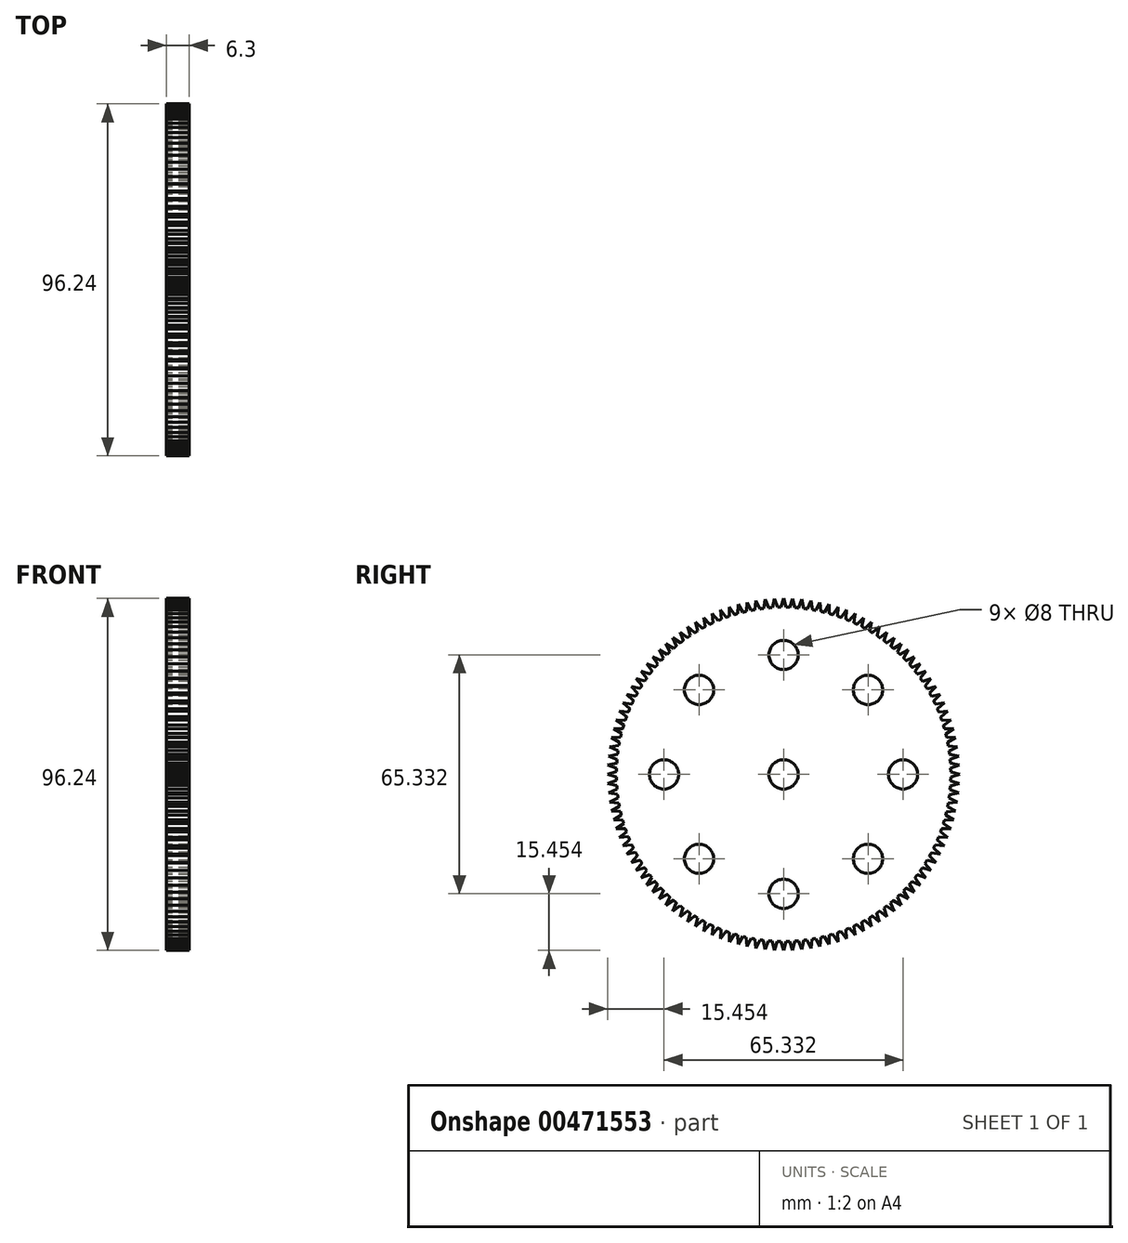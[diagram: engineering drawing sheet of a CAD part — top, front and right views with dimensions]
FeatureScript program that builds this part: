
annotation { "Feature Type Name" : "Feature", "Feature Type Description" : "" }
export const myFeature = defineFeature(function(context is Context, id is Id, definition is map)
    precondition{}
    {
        {
            var Q0;
            Q0=qCreatedBy(makeId("Right.planeOp"),FACE);
            var sketch = newSketch(context, id + "F0", { "sketchPlane" : qUnion([Q0])});
            skCircle(sketch, "E0", {"center": v(0, 0) * mm, "radius": 45.72 * mm});
            skCircle(sketch, "E1", {"center": v(0, 32.67) * mm, "radius": 4 * mm});
            skCircle(sketch, "E2.1.0", {"center": v(-23.1, 23.1) * mm, "radius": 4 * mm});
            skCircle(sketch, "E2.2.0", {"center": v(-32.67, 0) * mm, "radius": 4 * mm});
            skCircle(sketch, "E2.3.0", {"center": v(-23.1, -23.1) * mm, "radius": 4 * mm});
            skCircle(sketch, "E2.4.0", {"center": v(0, -32.67) * mm, "radius": 4 * mm});
            skCircle(sketch, "E2.5.0", {"center": v(23.1, -23.1) * mm, "radius": 4 * mm});
            skCircle(sketch, "E2.6.0", {"center": v(32.67, 0) * mm, "radius": 4 * mm});
            skCircle(sketch, "E2.7.0", {"center": v(23.1, 23.1) * mm, "radius": 4 * mm});
            skCircle(sketch, "E3", {"center": v(0, 0) * mm, "radius": 4 * mm});
            skSolve(sketch);
        }
        {
            var Q0;
            Q0=makeQuery(id+"F0.imprint","IMPRINT",FACE,{"disambiguationData":[TD([[makeQuery(id+"F0.imprint","IMPRINT",EDGE,{"derivedFrom":sQuery(id+"F0.wireOp",EDGE,"E0")}),1.0]])]});
            extrude(context, id + "F1", {"entities" : qUnion([Q0]), "depth" : 6.3 * mm});
        }
        {
            var Q0;
            Q0=qCreatedBy(makeId("Right.planeOp"),FACE);
            var sketch = newSketch(context, id + "F2", { "sketchPlane" : qUnion([Q0])});
            skLineSegment(sketch, "E4", {"start": v(-45.69, 0.74) * mm, "end": v(-48.12, 0) * mm});
            skLineSegment(sketch, "E5", {"start": v(-48.12, 0) * mm, "end": v(-45.69, -0.69) * mm});
            skLineSegment(sketch, "E6.1.0", {"start": v(-45.67, -1.65) * mm, "end": v(-48.06, -2.52) * mm});
            skLineSegment(sketch, "E6.2.0", {"start": v(-45.52, -4.04) * mm, "end": v(-47.86, -5.03) * mm});
            skLineSegment(sketch, "E6.3.0", {"start": v(-45.24, -6.42) * mm, "end": v(-47.53, -7.53) * mm});
            skLineSegment(sketch, "E6.4.0", {"start": v(-44.85, -8.78) * mm, "end": v(-47.07, -10) * mm});
            skLineSegment(sketch, "E6.5.0", {"start": v(-44.32, -11.11) * mm, "end": v(-46.48, -12.46) * mm});
            skLineSegment(sketch, "E6.6.0", {"start": v(-43.68, -13.42) * mm, "end": v(-45.77, -14.87) * mm});
            skLineSegment(sketch, "E6.7.0", {"start": v(-42.92, -15.68) * mm, "end": v(-44.93, -17.25) * mm});
            skLineSegment(sketch, "E6.8.0", {"start": v(-42.04, -17.9) * mm, "end": v(-43.96, -19.57) * mm});
            skLineSegment(sketch, "E6.9.0", {"start": v(-41.05, -20.08) * mm, "end": v(-42.88, -21.85) * mm});
            skLineSegment(sketch, "E6.10.0", {"start": v(-39.94, -22.2) * mm, "end": v(-41.68, -24.06) * mm});
            skLineSegment(sketch, "E6.11.0", {"start": v(-38.72, -24.26) * mm, "end": v(-40.36, -26.21) * mm});
            skLineSegment(sketch, "E6.12.0", {"start": v(-37.4, -26.26) * mm, "end": v(-38.93, -28.29) * mm});
            skLineSegment(sketch, "E6.13.0", {"start": v(-35.97, -28.18) * mm, "end": v(-37.4, -30.29) * mm});
            skLineSegment(sketch, "E6.14.0", {"start": v(-34.45, -30.02) * mm, "end": v(-35.76, -32.2) * mm});
            skLineSegment(sketch, "E6.15.0", {"start": v(-32.83, -31.78) * mm, "end": v(-34.03, -34.03) * mm});
            skLineSegment(sketch, "E6.16.0", {"start": v(-31.12, -33.46) * mm, "end": v(-32.2, -35.76) * mm});
            skLineSegment(sketch, "E6.17.0", {"start": v(-29.33, -35.04) * mm, "end": v(-30.29, -37.4) * mm});
            skLineSegment(sketch, "E6.18.0", {"start": v(-27.45, -36.53) * mm, "end": v(-28.29, -38.93) * mm});
            skLineSegment(sketch, "E6.19.0", {"start": v(-25.5, -37.92) * mm, "end": v(-26.21, -40.36) * mm});
            skLineSegment(sketch, "E6.20.0", {"start": v(-23.49, -39.2) * mm, "end": v(-24.06, -41.68) * mm});
            skLineSegment(sketch, "E6.21.0", {"start": v(-21.4, -40.37) * mm, "end": v(-21.85, -42.88) * mm});
            skLineSegment(sketch, "E6.22.0", {"start": v(-19.26, -41.44) * mm, "end": v(-19.57, -43.96) * mm});
            skLineSegment(sketch, "E6.23.0", {"start": v(-17.06, -42.4) * mm, "end": v(-17.25, -44.93) * mm});
            skLineSegment(sketch, "E6.24.0", {"start": v(-14.82, -43.23) * mm, "end": v(-14.87, -45.77) * mm});
            skLineSegment(sketch, "E6.25.0", {"start": v(-12.54, -43.94) * mm, "end": v(-12.46, -46.48) * mm});
            skLineSegment(sketch, "E6.26.0", {"start": v(-10.22, -44.54) * mm, "end": v(-10, -47.07) * mm});
            skLineSegment(sketch, "E6.27.0", {"start": v(-7.88, -45.01) * mm, "end": v(-7.53, -47.53) * mm});
            skLineSegment(sketch, "E6.28.0", {"start": v(-5.51, -45.36) * mm, "end": v(-5.03, -47.86) * mm});
            skLineSegment(sketch, "E6.29.0", {"start": v(-3.13, -45.59) * mm, "end": v(-2.52, -48.06) * mm});
            skLineSegment(sketch, "E6.30.0", {"start": v(-0.74, -45.69) * mm, "end": v(0, -48.12) * mm});
            skLineSegment(sketch, "E6.31.0", {"start": v(1.65, -45.67) * mm, "end": v(2.52, -48.06) * mm});
            skLineSegment(sketch, "E6.32.0", {"start": v(4.04, -45.52) * mm, "end": v(5.03, -47.86) * mm});
            skLineSegment(sketch, "E6.33.0", {"start": v(6.42, -45.24) * mm, "end": v(7.53, -47.53) * mm});
            skLineSegment(sketch, "E6.34.0", {"start": v(8.78, -44.85) * mm, "end": v(10, -47.07) * mm});
            skLineSegment(sketch, "E6.35.0", {"start": v(11.11, -44.32) * mm, "end": v(12.46, -46.48) * mm});
            skLineSegment(sketch, "E6.36.0", {"start": v(13.42, -43.68) * mm, "end": v(14.87, -45.77) * mm});
            skLineSegment(sketch, "E6.37.0", {"start": v(15.68, -42.92) * mm, "end": v(17.25, -44.93) * mm});
            skLineSegment(sketch, "E6.38.0", {"start": v(17.9, -42.04) * mm, "end": v(19.57, -43.96) * mm});
            skLineSegment(sketch, "E6.39.0", {"start": v(20.08, -41.05) * mm, "end": v(21.85, -42.88) * mm});
            skLineSegment(sketch, "E6.40.0", {"start": v(22.2, -39.94) * mm, "end": v(24.06, -41.68) * mm});
            skLineSegment(sketch, "E6.41.0", {"start": v(24.26, -38.72) * mm, "end": v(26.21, -40.36) * mm});
            skLineSegment(sketch, "E6.42.0", {"start": v(26.26, -37.4) * mm, "end": v(28.29, -38.93) * mm});
            skLineSegment(sketch, "E6.43.0", {"start": v(28.18, -35.97) * mm, "end": v(30.29, -37.4) * mm});
            skLineSegment(sketch, "E6.44.0", {"start": v(30.02, -34.45) * mm, "end": v(32.2, -35.76) * mm});
            skLineSegment(sketch, "E6.45.0", {"start": v(31.78, -32.83) * mm, "end": v(34.03, -34.03) * mm});
            skLineSegment(sketch, "E6.46.0", {"start": v(33.46, -31.12) * mm, "end": v(35.76, -32.2) * mm});
            skLineSegment(sketch, "E6.47.0", {"start": v(35.04, -29.33) * mm, "end": v(37.4, -30.29) * mm});
            skLineSegment(sketch, "E6.48.0", {"start": v(36.53, -27.45) * mm, "end": v(38.93, -28.29) * mm});
            skLineSegment(sketch, "E6.49.0", {"start": v(37.92, -25.5) * mm, "end": v(40.36, -26.21) * mm});
            skLineSegment(sketch, "E6.50.0", {"start": v(39.2, -23.49) * mm, "end": v(41.68, -24.06) * mm});
            skLineSegment(sketch, "E6.51.0", {"start": v(40.37, -21.4) * mm, "end": v(42.88, -21.85) * mm});
            skLineSegment(sketch, "E6.52.0", {"start": v(41.44, -19.26) * mm, "end": v(43.96, -19.57) * mm});
            skLineSegment(sketch, "E6.53.0", {"start": v(42.4, -17.06) * mm, "end": v(44.93, -17.25) * mm});
            skLineSegment(sketch, "E6.54.0", {"start": v(43.23, -14.82) * mm, "end": v(45.77, -14.87) * mm});
            skLineSegment(sketch, "E6.55.0", {"start": v(43.94, -12.54) * mm, "end": v(46.48, -12.46) * mm});
            skLineSegment(sketch, "E6.56.0", {"start": v(44.54, -10.22) * mm, "end": v(47.07, -10) * mm});
            skLineSegment(sketch, "E6.57.0", {"start": v(45.01, -7.88) * mm, "end": v(47.53, -7.53) * mm});
            skLineSegment(sketch, "E6.58.0", {"start": v(45.36, -5.51) * mm, "end": v(47.86, -5.03) * mm});
            skLineSegment(sketch, "E6.59.0", {"start": v(45.59, -3.13) * mm, "end": v(48.06, -2.52) * mm});
            skLineSegment(sketch, "E6.60.0", {"start": v(45.69, -0.74) * mm, "end": v(48.12, 0) * mm});
            skLineSegment(sketch, "E6.61.0", {"start": v(45.67, 1.65) * mm, "end": v(48.06, 2.52) * mm});
            skLineSegment(sketch, "E6.62.0", {"start": v(45.52, 4.04) * mm, "end": v(47.86, 5.03) * mm});
            skLineSegment(sketch, "E6.63.0", {"start": v(45.24, 6.42) * mm, "end": v(47.53, 7.53) * mm});
            skLineSegment(sketch, "E6.64.0", {"start": v(44.85, 8.78) * mm, "end": v(47.07, 10) * mm});
            skLineSegment(sketch, "E6.65.0", {"start": v(44.32, 11.11) * mm, "end": v(46.48, 12.46) * mm});
            skLineSegment(sketch, "E6.66.0", {"start": v(43.68, 13.42) * mm, "end": v(45.77, 14.87) * mm});
            skLineSegment(sketch, "E6.67.0", {"start": v(42.92, 15.68) * mm, "end": v(44.93, 17.25) * mm});
            skLineSegment(sketch, "E6.68.0", {"start": v(42.04, 17.9) * mm, "end": v(43.96, 19.57) * mm});
            skLineSegment(sketch, "E6.69.0", {"start": v(41.05, 20.08) * mm, "end": v(42.88, 21.85) * mm});
            skLineSegment(sketch, "E6.70.0", {"start": v(39.94, 22.2) * mm, "end": v(41.68, 24.06) * mm});
            skLineSegment(sketch, "E6.71.0", {"start": v(38.72, 24.26) * mm, "end": v(40.36, 26.21) * mm});
            skLineSegment(sketch, "E6.72.0", {"start": v(37.4, 26.26) * mm, "end": v(38.93, 28.29) * mm});
            skLineSegment(sketch, "E6.73.0", {"start": v(35.97, 28.18) * mm, "end": v(37.4, 30.29) * mm});
            skLineSegment(sketch, "E6.74.0", {"start": v(34.45, 30.02) * mm, "end": v(35.76, 32.2) * mm});
            skLineSegment(sketch, "E6.75.0", {"start": v(32.83, 31.78) * mm, "end": v(34.03, 34.03) * mm});
            skLineSegment(sketch, "E6.76.0", {"start": v(31.12, 33.46) * mm, "end": v(32.2, 35.76) * mm});
            skLineSegment(sketch, "E6.77.0", {"start": v(29.33, 35.04) * mm, "end": v(30.29, 37.4) * mm});
            skLineSegment(sketch, "E6.78.0", {"start": v(27.45, 36.53) * mm, "end": v(28.29, 38.93) * mm});
            skLineSegment(sketch, "E6.79.0", {"start": v(25.5, 37.92) * mm, "end": v(26.21, 40.36) * mm});
            skLineSegment(sketch, "E6.80.0", {"start": v(23.49, 39.2) * mm, "end": v(24.06, 41.68) * mm});
            skLineSegment(sketch, "E6.81.0", {"start": v(21.4, 40.37) * mm, "end": v(21.85, 42.88) * mm});
            skLineSegment(sketch, "E6.82.0", {"start": v(19.26, 41.44) * mm, "end": v(19.57, 43.96) * mm});
            skLineSegment(sketch, "E6.83.0", {"start": v(17.06, 42.4) * mm, "end": v(17.25, 44.93) * mm});
            skLineSegment(sketch, "E6.84.0", {"start": v(14.82, 43.23) * mm, "end": v(14.87, 45.77) * mm});
            skLineSegment(sketch, "E6.85.0", {"start": v(12.54, 43.94) * mm, "end": v(12.46, 46.48) * mm});
            skLineSegment(sketch, "E6.86.0", {"start": v(10.22, 44.54) * mm, "end": v(10, 47.07) * mm});
            skLineSegment(sketch, "E6.87.0", {"start": v(7.88, 45.01) * mm, "end": v(7.53, 47.53) * mm});
            skLineSegment(sketch, "E6.88.0", {"start": v(5.51, 45.36) * mm, "end": v(5.03, 47.86) * mm});
            skLineSegment(sketch, "E6.89.0", {"start": v(3.13, 45.59) * mm, "end": v(2.52, 48.06) * mm});
            skLineSegment(sketch, "E6.90.0", {"start": v(0.74, 45.69) * mm, "end": v(0, 48.12) * mm});
            skLineSegment(sketch, "E6.91.0", {"start": v(-1.65, 45.67) * mm, "end": v(-2.52, 48.06) * mm});
            skLineSegment(sketch, "E6.92.0", {"start": v(-4.04, 45.52) * mm, "end": v(-5.03, 47.86) * mm});
            skLineSegment(sketch, "E6.93.0", {"start": v(-6.42, 45.24) * mm, "end": v(-7.53, 47.53) * mm});
            skLineSegment(sketch, "E6.94.0", {"start": v(-8.78, 44.85) * mm, "end": v(-10, 47.07) * mm});
            skLineSegment(sketch, "E6.95.0", {"start": v(-11.11, 44.32) * mm, "end": v(-12.46, 46.48) * mm});
            skLineSegment(sketch, "E6.96.0", {"start": v(-13.42, 43.68) * mm, "end": v(-14.87, 45.77) * mm});
            skLineSegment(sketch, "E6.97.0", {"start": v(-15.68, 42.92) * mm, "end": v(-17.25, 44.93) * mm});
            skLineSegment(sketch, "E6.98.0", {"start": v(-17.9, 42.04) * mm, "end": v(-19.57, 43.96) * mm});
            skLineSegment(sketch, "E6.99.0", {"start": v(-20.08, 41.05) * mm, "end": v(-21.85, 42.88) * mm});
            skLineSegment(sketch, "E6.100.0", {"start": v(-22.2, 39.94) * mm, "end": v(-24.06, 41.68) * mm});
            skLineSegment(sketch, "E6.101.0", {"start": v(-24.26, 38.72) * mm, "end": v(-26.21, 40.36) * mm});
            skLineSegment(sketch, "E6.102.0", {"start": v(-26.26, 37.4) * mm, "end": v(-28.29, 38.93) * mm});
            skLineSegment(sketch, "E6.103.0", {"start": v(-28.18, 35.97) * mm, "end": v(-30.29, 37.4) * mm});
            skLineSegment(sketch, "E6.104.0", {"start": v(-30.02, 34.45) * mm, "end": v(-32.2, 35.76) * mm});
            skLineSegment(sketch, "E6.105.0", {"start": v(-31.78, 32.83) * mm, "end": v(-34.03, 34.03) * mm});
            skLineSegment(sketch, "E6.106.0", {"start": v(-33.46, 31.12) * mm, "end": v(-35.76, 32.2) * mm});
            skLineSegment(sketch, "E6.107.0", {"start": v(-35.04, 29.33) * mm, "end": v(-37.4, 30.29) * mm});
            skLineSegment(sketch, "E6.108.0", {"start": v(-36.53, 27.45) * mm, "end": v(-38.93, 28.29) * mm});
            skLineSegment(sketch, "E6.109.0", {"start": v(-37.92, 25.5) * mm, "end": v(-40.36, 26.21) * mm});
            skLineSegment(sketch, "E6.110.0", {"start": v(-39.2, 23.49) * mm, "end": v(-41.68, 24.06) * mm});
            skLineSegment(sketch, "E6.111.0", {"start": v(-40.37, 21.4) * mm, "end": v(-42.88, 21.85) * mm});
            skLineSegment(sketch, "E6.112.0", {"start": v(-41.44, 19.26) * mm, "end": v(-43.96, 19.57) * mm});
            skLineSegment(sketch, "E6.113.0", {"start": v(-42.4, 17.06) * mm, "end": v(-44.93, 17.25) * mm});
            skLineSegment(sketch, "E6.114.0", {"start": v(-43.23, 14.82) * mm, "end": v(-45.77, 14.87) * mm});
            skLineSegment(sketch, "E6.115.0", {"start": v(-43.94, 12.54) * mm, "end": v(-46.48, 12.46) * mm});
            skLineSegment(sketch, "E6.116.0", {"start": v(-44.54, 10.22) * mm, "end": v(-47.07, 10) * mm});
            skLineSegment(sketch, "E6.117.0", {"start": v(-45.01, 7.88) * mm, "end": v(-47.53, 7.53) * mm});
            skLineSegment(sketch, "E6.118.0", {"start": v(-45.36, 5.51) * mm, "end": v(-47.86, 5.03) * mm});
            skLineSegment(sketch, "E6.119.0", {"start": v(-45.59, 3.13) * mm, "end": v(-48.06, 2.52) * mm});
            skPoint(sketch, "E6.center", {"position": v(0, 0) * mm});
            skLineSegment(sketch, "E7.1.0", {"start": v(-48.06, -2.52) * mm, "end": v(-45.6, -3.08) * mm});
            skLineSegment(sketch, "E7.2.0", {"start": v(-47.86, -5.03) * mm, "end": v(-45.37, -5.46) * mm});
            skLineSegment(sketch, "E7.3.0", {"start": v(-47.53, -7.53) * mm, "end": v(-45.02, -7.82) * mm});
            skLineSegment(sketch, "E7.4.0", {"start": v(-47.07, -10) * mm, "end": v(-44.55, -10.17) * mm});
            skLineSegment(sketch, "E7.5.0", {"start": v(-46.48, -12.46) * mm, "end": v(-43.96, -12.49) * mm});
            skLineSegment(sketch, "E7.6.0", {"start": v(-45.77, -14.87) * mm, "end": v(-43.24, -14.77) * mm});
            skLineSegment(sketch, "E7.7.0", {"start": v(-44.93, -17.25) * mm, "end": v(-42.4, -17.01) * mm});
            skLineSegment(sketch, "E7.8.0", {"start": v(-43.96, -19.57) * mm, "end": v(-41.46, -19.21) * mm});
            skLineSegment(sketch, "E7.9.0", {"start": v(-42.88, -21.85) * mm, "end": v(-40.4, -21.35) * mm});
            skLineSegment(sketch, "E7.10.0", {"start": v(-41.68, -24.06) * mm, "end": v(-39.23, -23.44) * mm});
            skLineSegment(sketch, "E7.11.0", {"start": v(-40.36, -26.21) * mm, "end": v(-37.95, -25.46) * mm});
            skLineSegment(sketch, "E7.12.0", {"start": v(-38.93, -28.29) * mm, "end": v(-36.56, -27.41) * mm});
            skLineSegment(sketch, "E7.13.0", {"start": v(-37.4, -30.29) * mm, "end": v(-35.08, -29.29) * mm});
            skLineSegment(sketch, "E7.14.0", {"start": v(-35.76, -32.2) * mm, "end": v(-33.5, -31.08) * mm});
            skLineSegment(sketch, "E7.15.0", {"start": v(-34.03, -34.03) * mm, "end": v(-31.82, -32.8) * mm});
            skLineSegment(sketch, "E7.16.0", {"start": v(-32.2, -35.76) * mm, "end": v(-30.06, -34.41) * mm});
            skLineSegment(sketch, "E7.17.0", {"start": v(-30.29, -37.4) * mm, "end": v(-28.22, -35.94) * mm});
            skLineSegment(sketch, "E7.18.0", {"start": v(-28.29, -38.93) * mm, "end": v(-26.3, -37.37) * mm});
            skLineSegment(sketch, "E7.19.0", {"start": v(-26.21, -40.36) * mm, "end": v(-24.3, -38.7) * mm});
            skLineSegment(sketch, "E7.20.0", {"start": v(-24.06, -41.68) * mm, "end": v(-22.25, -39.91) * mm});
            skLineSegment(sketch, "E7.21.0", {"start": v(-21.85, -42.88) * mm, "end": v(-20.13, -41.02) * mm});
            skLineSegment(sketch, "E7.22.0", {"start": v(-19.57, -43.96) * mm, "end": v(-17.96, -42.02) * mm});
            skLineSegment(sketch, "E7.23.0", {"start": v(-17.25, -44.93) * mm, "end": v(-15.73, -42.9) * mm});
            skLineSegment(sketch, "E7.24.0", {"start": v(-14.87, -45.77) * mm, "end": v(-13.47, -43.67) * mm});
            skLineSegment(sketch, "E7.25.0", {"start": v(-12.46, -46.48) * mm, "end": v(-11.16, -44.31) * mm});
            skLineSegment(sketch, "E7.26.0", {"start": v(-10, -47.07) * mm, "end": v(-8.83, -44.83) * mm});
            skLineSegment(sketch, "E7.27.0", {"start": v(-7.53, -47.53) * mm, "end": v(-6.47, -45.23) * mm});
            skLineSegment(sketch, "E7.28.0", {"start": v(-5.03, -47.86) * mm, "end": v(-4.1, -45.51) * mm});
            skLineSegment(sketch, "E7.29.0", {"start": v(-2.52, -48.06) * mm, "end": v(-1.7, -45.66) * mm});
            skLineSegment(sketch, "E7.30.0", {"start": v(0, -48.12) * mm, "end": v(0.69, -45.69) * mm});
            skLineSegment(sketch, "E7.31.0", {"start": v(2.52, -48.06) * mm, "end": v(3.08, -45.6) * mm});
            skLineSegment(sketch, "E7.32.0", {"start": v(5.03, -47.86) * mm, "end": v(5.46, -45.37) * mm});
            skLineSegment(sketch, "E7.33.0", {"start": v(7.53, -47.53) * mm, "end": v(7.82, -45.02) * mm});
            skLineSegment(sketch, "E7.34.0", {"start": v(10, -47.07) * mm, "end": v(10.17, -44.55) * mm});
            skLineSegment(sketch, "E7.35.0", {"start": v(12.46, -46.48) * mm, "end": v(12.49, -43.96) * mm});
            skLineSegment(sketch, "E7.36.0", {"start": v(14.87, -45.77) * mm, "end": v(14.77, -43.24) * mm});
            skLineSegment(sketch, "E7.37.0", {"start": v(17.25, -44.93) * mm, "end": v(17.01, -42.4) * mm});
            skLineSegment(sketch, "E7.38.0", {"start": v(19.57, -43.96) * mm, "end": v(19.21, -41.46) * mm});
            skLineSegment(sketch, "E7.39.0", {"start": v(21.85, -42.88) * mm, "end": v(21.35, -40.4) * mm});
            skLineSegment(sketch, "E7.40.0", {"start": v(24.06, -41.68) * mm, "end": v(23.44, -39.23) * mm});
            skLineSegment(sketch, "E7.41.0", {"start": v(26.21, -40.36) * mm, "end": v(25.46, -37.95) * mm});
            skLineSegment(sketch, "E7.42.0", {"start": v(28.29, -38.93) * mm, "end": v(27.41, -36.56) * mm});
            skLineSegment(sketch, "E7.43.0", {"start": v(30.29, -37.4) * mm, "end": v(29.29, -35.08) * mm});
            skLineSegment(sketch, "E7.44.0", {"start": v(32.2, -35.76) * mm, "end": v(31.08, -33.5) * mm});
            skLineSegment(sketch, "E7.45.0", {"start": v(34.03, -34.03) * mm, "end": v(32.8, -31.82) * mm});
            skLineSegment(sketch, "E7.46.0", {"start": v(35.76, -32.2) * mm, "end": v(34.41, -30.06) * mm});
            skLineSegment(sketch, "E7.47.0", {"start": v(37.4, -30.29) * mm, "end": v(35.94, -28.22) * mm});
            skLineSegment(sketch, "E7.48.0", {"start": v(38.93, -28.29) * mm, "end": v(37.37, -26.3) * mm});
            skLineSegment(sketch, "E7.49.0", {"start": v(40.36, -26.21) * mm, "end": v(38.7, -24.3) * mm});
            skLineSegment(sketch, "E7.50.0", {"start": v(41.68, -24.06) * mm, "end": v(39.91, -22.25) * mm});
            skLineSegment(sketch, "E7.51.0", {"start": v(42.88, -21.85) * mm, "end": v(41.02, -20.13) * mm});
            skLineSegment(sketch, "E7.52.0", {"start": v(43.96, -19.57) * mm, "end": v(42.02, -17.96) * mm});
            skLineSegment(sketch, "E7.53.0", {"start": v(44.93, -17.25) * mm, "end": v(42.9, -15.73) * mm});
            skLineSegment(sketch, "E7.54.0", {"start": v(45.77, -14.87) * mm, "end": v(43.67, -13.47) * mm});
            skLineSegment(sketch, "E7.55.0", {"start": v(46.48, -12.46) * mm, "end": v(44.31, -11.16) * mm});
            skLineSegment(sketch, "E7.56.0", {"start": v(47.07, -10) * mm, "end": v(44.83, -8.83) * mm});
            skLineSegment(sketch, "E7.57.0", {"start": v(47.53, -7.53) * mm, "end": v(45.23, -6.47) * mm});
            skLineSegment(sketch, "E7.58.0", {"start": v(47.86, -5.03) * mm, "end": v(45.51, -4.1) * mm});
            skLineSegment(sketch, "E7.59.0", {"start": v(48.06, -2.52) * mm, "end": v(45.66, -1.7) * mm});
            skLineSegment(sketch, "E7.60.0", {"start": v(48.12, 0) * mm, "end": v(45.69, 0.69) * mm});
            skLineSegment(sketch, "E7.61.0", {"start": v(48.06, 2.52) * mm, "end": v(45.6, 3.08) * mm});
            skLineSegment(sketch, "E7.62.0", {"start": v(47.86, 5.03) * mm, "end": v(45.37, 5.46) * mm});
            skLineSegment(sketch, "E7.63.0", {"start": v(47.53, 7.53) * mm, "end": v(45.02, 7.82) * mm});
            skLineSegment(sketch, "E7.64.0", {"start": v(47.07, 10) * mm, "end": v(44.55, 10.17) * mm});
            skLineSegment(sketch, "E7.65.0", {"start": v(46.48, 12.46) * mm, "end": v(43.96, 12.49) * mm});
            skLineSegment(sketch, "E7.66.0", {"start": v(45.77, 14.87) * mm, "end": v(43.24, 14.77) * mm});
            skLineSegment(sketch, "E7.67.0", {"start": v(44.93, 17.25) * mm, "end": v(42.4, 17.01) * mm});
            skLineSegment(sketch, "E7.68.0", {"start": v(43.96, 19.57) * mm, "end": v(41.46, 19.21) * mm});
            skLineSegment(sketch, "E7.69.0", {"start": v(42.88, 21.85) * mm, "end": v(40.4, 21.35) * mm});
            skLineSegment(sketch, "E7.70.0", {"start": v(41.68, 24.06) * mm, "end": v(39.23, 23.44) * mm});
            skLineSegment(sketch, "E7.71.0", {"start": v(40.36, 26.21) * mm, "end": v(37.95, 25.46) * mm});
            skLineSegment(sketch, "E7.72.0", {"start": v(38.93, 28.29) * mm, "end": v(36.56, 27.41) * mm});
            skLineSegment(sketch, "E7.73.0", {"start": v(37.4, 30.29) * mm, "end": v(35.08, 29.29) * mm});
            skLineSegment(sketch, "E7.74.0", {"start": v(35.76, 32.2) * mm, "end": v(33.5, 31.08) * mm});
            skLineSegment(sketch, "E7.75.0", {"start": v(34.03, 34.03) * mm, "end": v(31.82, 32.8) * mm});
            skLineSegment(sketch, "E7.76.0", {"start": v(32.2, 35.76) * mm, "end": v(30.06, 34.41) * mm});
            skLineSegment(sketch, "E7.77.0", {"start": v(30.29, 37.4) * mm, "end": v(28.22, 35.94) * mm});
            skLineSegment(sketch, "E7.78.0", {"start": v(28.29, 38.93) * mm, "end": v(26.3, 37.37) * mm});
            skLineSegment(sketch, "E7.79.0", {"start": v(26.21, 40.36) * mm, "end": v(24.3, 38.7) * mm});
            skLineSegment(sketch, "E7.80.0", {"start": v(24.06, 41.68) * mm, "end": v(22.25, 39.91) * mm});
            skLineSegment(sketch, "E7.81.0", {"start": v(21.85, 42.88) * mm, "end": v(20.13, 41.02) * mm});
            skLineSegment(sketch, "E7.82.0", {"start": v(19.57, 43.96) * mm, "end": v(17.96, 42.02) * mm});
            skLineSegment(sketch, "E7.83.0", {"start": v(17.25, 44.93) * mm, "end": v(15.73, 42.9) * mm});
            skLineSegment(sketch, "E7.84.0", {"start": v(14.87, 45.77) * mm, "end": v(13.47, 43.67) * mm});
            skLineSegment(sketch, "E7.85.0", {"start": v(12.46, 46.48) * mm, "end": v(11.16, 44.31) * mm});
            skLineSegment(sketch, "E7.86.0", {"start": v(10, 47.07) * mm, "end": v(8.83, 44.83) * mm});
            skLineSegment(sketch, "E7.87.0", {"start": v(7.53, 47.53) * mm, "end": v(6.47, 45.23) * mm});
            skLineSegment(sketch, "E7.88.0", {"start": v(5.03, 47.86) * mm, "end": v(4.1, 45.51) * mm});
            skLineSegment(sketch, "E7.89.0", {"start": v(2.52, 48.06) * mm, "end": v(1.7, 45.66) * mm});
            skLineSegment(sketch, "E7.90.0", {"start": v(0, 48.12) * mm, "end": v(-0.69, 45.69) * mm});
            skLineSegment(sketch, "E7.91.0", {"start": v(-2.52, 48.06) * mm, "end": v(-3.08, 45.6) * mm});
            skLineSegment(sketch, "E7.92.0", {"start": v(-5.03, 47.86) * mm, "end": v(-5.46, 45.37) * mm});
            skLineSegment(sketch, "E7.93.0", {"start": v(-7.53, 47.53) * mm, "end": v(-7.82, 45.02) * mm});
            skLineSegment(sketch, "E7.94.0", {"start": v(-10, 47.07) * mm, "end": v(-10.17, 44.55) * mm});
            skLineSegment(sketch, "E7.95.0", {"start": v(-12.46, 46.48) * mm, "end": v(-12.49, 43.96) * mm});
            skLineSegment(sketch, "E7.96.0", {"start": v(-14.87, 45.77) * mm, "end": v(-14.77, 43.24) * mm});
            skLineSegment(sketch, "E7.97.0", {"start": v(-17.25, 44.93) * mm, "end": v(-17.01, 42.4) * mm});
            skLineSegment(sketch, "E7.98.0", {"start": v(-19.57, 43.96) * mm, "end": v(-19.21, 41.46) * mm});
            skLineSegment(sketch, "E7.99.0", {"start": v(-21.85, 42.88) * mm, "end": v(-21.35, 40.4) * mm});
            skLineSegment(sketch, "E7.100.0", {"start": v(-24.06, 41.68) * mm, "end": v(-23.44, 39.23) * mm});
            skLineSegment(sketch, "E7.101.0", {"start": v(-26.21, 40.36) * mm, "end": v(-25.46, 37.95) * mm});
            skLineSegment(sketch, "E7.102.0", {"start": v(-28.29, 38.93) * mm, "end": v(-27.41, 36.56) * mm});
            skLineSegment(sketch, "E7.103.0", {"start": v(-30.29, 37.4) * mm, "end": v(-29.29, 35.08) * mm});
            skLineSegment(sketch, "E7.104.0", {"start": v(-32.2, 35.76) * mm, "end": v(-31.08, 33.5) * mm});
            skLineSegment(sketch, "E7.105.0", {"start": v(-34.03, 34.03) * mm, "end": v(-32.8, 31.82) * mm});
            skLineSegment(sketch, "E7.106.0", {"start": v(-35.76, 32.2) * mm, "end": v(-34.41, 30.06) * mm});
            skLineSegment(sketch, "E7.107.0", {"start": v(-37.4, 30.29) * mm, "end": v(-35.94, 28.22) * mm});
            skLineSegment(sketch, "E7.108.0", {"start": v(-38.93, 28.29) * mm, "end": v(-37.37, 26.3) * mm});
            skLineSegment(sketch, "E7.109.0", {"start": v(-40.36, 26.21) * mm, "end": v(-38.7, 24.3) * mm});
            skLineSegment(sketch, "E7.110.0", {"start": v(-41.68, 24.06) * mm, "end": v(-39.91, 22.25) * mm});
            skLineSegment(sketch, "E7.111.0", {"start": v(-42.88, 21.85) * mm, "end": v(-41.02, 20.13) * mm});
            skLineSegment(sketch, "E7.112.0", {"start": v(-43.96, 19.57) * mm, "end": v(-42.02, 17.96) * mm});
            skLineSegment(sketch, "E7.113.0", {"start": v(-44.93, 17.25) * mm, "end": v(-42.9, 15.73) * mm});
            skLineSegment(sketch, "E7.114.0", {"start": v(-45.77, 14.87) * mm, "end": v(-43.67, 13.47) * mm});
            skLineSegment(sketch, "E7.115.0", {"start": v(-46.48, 12.46) * mm, "end": v(-44.31, 11.16) * mm});
            skLineSegment(sketch, "E7.116.0", {"start": v(-47.07, 10) * mm, "end": v(-44.83, 8.83) * mm});
            skLineSegment(sketch, "E7.117.0", {"start": v(-47.53, 7.53) * mm, "end": v(-45.23, 6.47) * mm});
            skLineSegment(sketch, "E7.118.0", {"start": v(-47.86, 5.03) * mm, "end": v(-45.51, 4.1) * mm});
            skLineSegment(sketch, "E7.119.0", {"start": v(-48.06, 2.52) * mm, "end": v(-45.66, 1.7) * mm});
            skLineSegment(sketch, "E8", {"start": v(22.25, 39.91) * mm, "end": v(23.49, 39.2) * mm});
            skLineSegment(sketch, "E9.1.0", {"start": v(20.13, 41.02) * mm, "end": v(21.4, 40.37) * mm});
            skLineSegment(sketch, "E9.2.0", {"start": v(17.96, 42.02) * mm, "end": v(19.26, 41.44) * mm});
            skLineSegment(sketch, "E9.3.0", {"start": v(15.73, 42.9) * mm, "end": v(17.06, 42.4) * mm});
            skLineSegment(sketch, "E9.4.0", {"start": v(13.47, 43.67) * mm, "end": v(14.82, 43.23) * mm});
            skLineSegment(sketch, "E9.5.0", {"start": v(11.16, 44.31) * mm, "end": v(12.54, 43.94) * mm});
            skLineSegment(sketch, "E9.6.0", {"start": v(8.83, 44.83) * mm, "end": v(10.22, 44.54) * mm});
            skLineSegment(sketch, "E9.7.0", {"start": v(6.47, 45.23) * mm, "end": v(7.88, 45.01) * mm});
            skLineSegment(sketch, "E9.8.0", {"start": v(4.1, 45.51) * mm, "end": v(5.51, 45.36) * mm});
            skLineSegment(sketch, "E9.9.0", {"start": v(1.7, 45.66) * mm, "end": v(3.13, 45.59) * mm});
            skLineSegment(sketch, "E9.10.0", {"start": v(-0.69, 45.69) * mm, "end": v(0.74, 45.69) * mm});
            skLineSegment(sketch, "E9.11.0", {"start": v(-3.08, 45.6) * mm, "end": v(-1.65, 45.67) * mm});
            skLineSegment(sketch, "E9.12.0", {"start": v(-5.46, 45.37) * mm, "end": v(-4.04, 45.52) * mm});
            skLineSegment(sketch, "E9.13.0", {"start": v(-7.82, 45.02) * mm, "end": v(-6.42, 45.24) * mm});
            skLineSegment(sketch, "E9.14.0", {"start": v(-10.17, 44.55) * mm, "end": v(-8.78, 44.85) * mm});
            skLineSegment(sketch, "E9.15.0", {"start": v(-12.49, 43.96) * mm, "end": v(-11.11, 44.32) * mm});
            skLineSegment(sketch, "E9.16.0", {"start": v(-14.77, 43.24) * mm, "end": v(-13.42, 43.68) * mm});
            skLineSegment(sketch, "E9.17.0", {"start": v(-17.01, 42.4) * mm, "end": v(-15.68, 42.92) * mm});
            skLineSegment(sketch, "E9.18.0", {"start": v(-19.21, 41.46) * mm, "end": v(-17.9, 42.04) * mm});
            skLineSegment(sketch, "E9.19.0", {"start": v(-21.35, 40.4) * mm, "end": v(-20.08, 41.05) * mm});
            skLineSegment(sketch, "E9.20.0", {"start": v(-23.44, 39.23) * mm, "end": v(-22.2, 39.94) * mm});
            skLineSegment(sketch, "E9.21.0", {"start": v(-25.46, 37.95) * mm, "end": v(-24.26, 38.72) * mm});
            skLineSegment(sketch, "E9.22.0", {"start": v(-27.41, 36.56) * mm, "end": v(-26.26, 37.4) * mm});
            skLineSegment(sketch, "E9.23.0", {"start": v(-29.29, 35.08) * mm, "end": v(-28.18, 35.97) * mm});
            skLineSegment(sketch, "E9.24.0", {"start": v(-31.08, 33.5) * mm, "end": v(-30.02, 34.45) * mm});
            skLineSegment(sketch, "E9.25.0", {"start": v(-32.8, 31.82) * mm, "end": v(-31.78, 32.83) * mm});
            skLineSegment(sketch, "E9.26.0", {"start": v(-34.41, 30.06) * mm, "end": v(-33.46, 31.12) * mm});
            skLineSegment(sketch, "E9.27.0", {"start": v(-35.94, 28.22) * mm, "end": v(-35.04, 29.33) * mm});
            skLineSegment(sketch, "E9.28.0", {"start": v(-37.37, 26.3) * mm, "end": v(-36.53, 27.45) * mm});
            skLineSegment(sketch, "E9.29.0", {"start": v(-38.7, 24.3) * mm, "end": v(-37.92, 25.5) * mm});
            skLineSegment(sketch, "E9.30.0", {"start": v(-39.91, 22.25) * mm, "end": v(-39.2, 23.49) * mm});
            skLineSegment(sketch, "E9.31.0", {"start": v(-41.02, 20.13) * mm, "end": v(-40.37, 21.4) * mm});
            skLineSegment(sketch, "E9.32.0", {"start": v(-42.02, 17.96) * mm, "end": v(-41.44, 19.26) * mm});
            skLineSegment(sketch, "E9.33.0", {"start": v(-42.9, 15.73) * mm, "end": v(-42.4, 17.06) * mm});
            skLineSegment(sketch, "E9.34.0", {"start": v(-43.67, 13.47) * mm, "end": v(-43.23, 14.82) * mm});
            skLineSegment(sketch, "E9.35.0", {"start": v(-44.31, 11.16) * mm, "end": v(-43.94, 12.54) * mm});
            skLineSegment(sketch, "E9.36.0", {"start": v(-44.83, 8.83) * mm, "end": v(-44.54, 10.22) * mm});
            skLineSegment(sketch, "E9.37.0", {"start": v(-45.23, 6.47) * mm, "end": v(-45.01, 7.88) * mm});
            skLineSegment(sketch, "E9.38.0", {"start": v(-45.51, 4.1) * mm, "end": v(-45.36, 5.51) * mm});
            skLineSegment(sketch, "E9.39.0", {"start": v(-45.66, 1.7) * mm, "end": v(-45.59, 3.13) * mm});
            skLineSegment(sketch, "E9.40.0", {"start": v(-45.69, -0.69) * mm, "end": v(-45.69, 0.74) * mm});
            skLineSegment(sketch, "E9.41.0", {"start": v(-45.6, -3.08) * mm, "end": v(-45.67, -1.65) * mm});
            skLineSegment(sketch, "E9.42.0", {"start": v(-45.37, -5.46) * mm, "end": v(-45.52, -4.04) * mm});
            skLineSegment(sketch, "E9.43.0", {"start": v(-45.02, -7.82) * mm, "end": v(-45.24, -6.42) * mm});
            skLineSegment(sketch, "E9.44.0", {"start": v(-44.55, -10.17) * mm, "end": v(-44.85, -8.78) * mm});
            skLineSegment(sketch, "E9.45.0", {"start": v(-43.96, -12.49) * mm, "end": v(-44.32, -11.11) * mm});
            skLineSegment(sketch, "E9.46.0", {"start": v(-43.24, -14.77) * mm, "end": v(-43.68, -13.42) * mm});
            skLineSegment(sketch, "E9.47.0", {"start": v(-42.4, -17.01) * mm, "end": v(-42.92, -15.68) * mm});
            skLineSegment(sketch, "E9.48.0", {"start": v(-41.46, -19.21) * mm, "end": v(-42.04, -17.9) * mm});
            skLineSegment(sketch, "E9.49.0", {"start": v(-40.4, -21.35) * mm, "end": v(-41.05, -20.08) * mm});
            skLineSegment(sketch, "E9.50.0", {"start": v(-39.23, -23.44) * mm, "end": v(-39.94, -22.2) * mm});
            skLineSegment(sketch, "E9.51.0", {"start": v(-37.95, -25.46) * mm, "end": v(-38.72, -24.26) * mm});
            skLineSegment(sketch, "E9.52.0", {"start": v(-36.56, -27.41) * mm, "end": v(-37.4, -26.26) * mm});
            skLineSegment(sketch, "E9.53.0", {"start": v(-35.08, -29.29) * mm, "end": v(-35.97, -28.18) * mm});
            skLineSegment(sketch, "E9.54.0", {"start": v(-33.5, -31.08) * mm, "end": v(-34.45, -30.02) * mm});
            skLineSegment(sketch, "E9.55.0", {"start": v(-31.82, -32.8) * mm, "end": v(-32.83, -31.78) * mm});
            skLineSegment(sketch, "E9.56.0", {"start": v(-30.06, -34.41) * mm, "end": v(-31.12, -33.46) * mm});
            skLineSegment(sketch, "E9.57.0", {"start": v(-28.22, -35.94) * mm, "end": v(-29.33, -35.04) * mm});
            skLineSegment(sketch, "E9.58.0", {"start": v(-26.3, -37.37) * mm, "end": v(-27.45, -36.53) * mm});
            skLineSegment(sketch, "E9.59.0", {"start": v(-24.3, -38.7) * mm, "end": v(-25.5, -37.92) * mm});
            skLineSegment(sketch, "E9.60.0", {"start": v(-22.25, -39.91) * mm, "end": v(-23.49, -39.2) * mm});
            skLineSegment(sketch, "E9.61.0", {"start": v(-20.13, -41.02) * mm, "end": v(-21.4, -40.37) * mm});
            skLineSegment(sketch, "E9.62.0", {"start": v(-17.96, -42.02) * mm, "end": v(-19.26, -41.44) * mm});
            skLineSegment(sketch, "E9.63.0", {"start": v(-15.73, -42.9) * mm, "end": v(-17.06, -42.4) * mm});
            skLineSegment(sketch, "E9.64.0", {"start": v(-13.47, -43.67) * mm, "end": v(-14.82, -43.23) * mm});
            skLineSegment(sketch, "E9.65.0", {"start": v(-11.16, -44.31) * mm, "end": v(-12.54, -43.94) * mm});
            skLineSegment(sketch, "E9.66.0", {"start": v(-8.83, -44.83) * mm, "end": v(-10.22, -44.54) * mm});
            skLineSegment(sketch, "E9.67.0", {"start": v(-6.47, -45.23) * mm, "end": v(-7.88, -45.01) * mm});
            skLineSegment(sketch, "E9.68.0", {"start": v(-4.1, -45.51) * mm, "end": v(-5.51, -45.36) * mm});
            skLineSegment(sketch, "E9.69.0", {"start": v(-1.7, -45.66) * mm, "end": v(-3.13, -45.59) * mm});
            skLineSegment(sketch, "E9.70.0", {"start": v(0.69, -45.69) * mm, "end": v(-0.74, -45.69) * mm});
            skLineSegment(sketch, "E9.71.0", {"start": v(3.08, -45.6) * mm, "end": v(1.65, -45.67) * mm});
            skLineSegment(sketch, "E9.72.0", {"start": v(5.46, -45.37) * mm, "end": v(4.04, -45.52) * mm});
            skLineSegment(sketch, "E9.73.0", {"start": v(7.82, -45.02) * mm, "end": v(6.42, -45.24) * mm});
            skLineSegment(sketch, "E9.74.0", {"start": v(10.17, -44.55) * mm, "end": v(8.78, -44.85) * mm});
            skLineSegment(sketch, "E9.75.0", {"start": v(12.49, -43.96) * mm, "end": v(11.11, -44.32) * mm});
            skLineSegment(sketch, "E9.76.0", {"start": v(14.77, -43.24) * mm, "end": v(13.42, -43.68) * mm});
            skLineSegment(sketch, "E9.77.0", {"start": v(17.01, -42.4) * mm, "end": v(15.68, -42.92) * mm});
            skLineSegment(sketch, "E9.78.0", {"start": v(19.21, -41.46) * mm, "end": v(17.9, -42.04) * mm});
            skLineSegment(sketch, "E9.79.0", {"start": v(21.35, -40.4) * mm, "end": v(20.08, -41.05) * mm});
            skLineSegment(sketch, "E9.80.0", {"start": v(23.44, -39.23) * mm, "end": v(22.2, -39.94) * mm});
            skLineSegment(sketch, "E9.81.0", {"start": v(25.46, -37.95) * mm, "end": v(24.26, -38.72) * mm});
            skLineSegment(sketch, "E9.82.0", {"start": v(27.41, -36.56) * mm, "end": v(26.26, -37.4) * mm});
            skLineSegment(sketch, "E9.83.0", {"start": v(29.29, -35.08) * mm, "end": v(28.18, -35.97) * mm});
            skLineSegment(sketch, "E9.84.0", {"start": v(31.08, -33.5) * mm, "end": v(30.02, -34.45) * mm});
            skLineSegment(sketch, "E9.85.0", {"start": v(32.8, -31.82) * mm, "end": v(31.78, -32.83) * mm});
            skLineSegment(sketch, "E9.86.0", {"start": v(34.41, -30.06) * mm, "end": v(33.46, -31.12) * mm});
            skLineSegment(sketch, "E9.87.0", {"start": v(35.94, -28.22) * mm, "end": v(35.04, -29.33) * mm});
            skLineSegment(sketch, "E9.88.0", {"start": v(37.37, -26.3) * mm, "end": v(36.53, -27.45) * mm});
            skLineSegment(sketch, "E9.89.0", {"start": v(38.7, -24.3) * mm, "end": v(37.92, -25.5) * mm});
            skLineSegment(sketch, "E9.90.0", {"start": v(39.91, -22.25) * mm, "end": v(39.2, -23.49) * mm});
            skLineSegment(sketch, "E9.91.0", {"start": v(41.02, -20.13) * mm, "end": v(40.37, -21.4) * mm});
            skLineSegment(sketch, "E9.92.0", {"start": v(42.02, -17.96) * mm, "end": v(41.44, -19.26) * mm});
            skLineSegment(sketch, "E9.93.0", {"start": v(42.9, -15.73) * mm, "end": v(42.4, -17.06) * mm});
            skLineSegment(sketch, "E9.94.0", {"start": v(43.67, -13.47) * mm, "end": v(43.23, -14.82) * mm});
            skLineSegment(sketch, "E9.95.0", {"start": v(44.31, -11.16) * mm, "end": v(43.94, -12.54) * mm});
            skLineSegment(sketch, "E9.96.0", {"start": v(44.83, -8.83) * mm, "end": v(44.54, -10.22) * mm});
            skLineSegment(sketch, "E9.97.0", {"start": v(45.23, -6.47) * mm, "end": v(45.01, -7.88) * mm});
            skLineSegment(sketch, "E9.98.0", {"start": v(45.51, -4.1) * mm, "end": v(45.36, -5.51) * mm});
            skLineSegment(sketch, "E9.99.0", {"start": v(45.66, -1.7) * mm, "end": v(45.59, -3.13) * mm});
            skLineSegment(sketch, "E9.100.0", {"start": v(45.69, 0.69) * mm, "end": v(45.69, -0.74) * mm});
            skLineSegment(sketch, "E9.101.0", {"start": v(45.6, 3.08) * mm, "end": v(45.67, 1.65) * mm});
            skLineSegment(sketch, "E9.102.0", {"start": v(45.37, 5.46) * mm, "end": v(45.52, 4.04) * mm});
            skLineSegment(sketch, "E9.103.0", {"start": v(45.02, 7.82) * mm, "end": v(45.24, 6.42) * mm});
            skLineSegment(sketch, "E9.104.0", {"start": v(44.55, 10.17) * mm, "end": v(44.85, 8.78) * mm});
            skLineSegment(sketch, "E9.105.0", {"start": v(43.96, 12.49) * mm, "end": v(44.32, 11.11) * mm});
            skLineSegment(sketch, "E9.106.0", {"start": v(43.24, 14.77) * mm, "end": v(43.68, 13.42) * mm});
            skLineSegment(sketch, "E9.107.0", {"start": v(42.4, 17.01) * mm, "end": v(42.92, 15.68) * mm});
            skLineSegment(sketch, "E9.108.0", {"start": v(41.46, 19.21) * mm, "end": v(42.04, 17.9) * mm});
            skLineSegment(sketch, "E9.109.0", {"start": v(40.4, 21.35) * mm, "end": v(41.05, 20.08) * mm});
            skLineSegment(sketch, "E9.110.0", {"start": v(39.23, 23.44) * mm, "end": v(39.94, 22.2) * mm});
            skLineSegment(sketch, "E9.111.0", {"start": v(37.95, 25.46) * mm, "end": v(38.72, 24.26) * mm});
            skLineSegment(sketch, "E9.112.0", {"start": v(36.56, 27.41) * mm, "end": v(37.4, 26.26) * mm});
            skLineSegment(sketch, "E9.113.0", {"start": v(35.08, 29.29) * mm, "end": v(35.97, 28.18) * mm});
            skLineSegment(sketch, "E9.114.0", {"start": v(33.5, 31.08) * mm, "end": v(34.45, 30.02) * mm});
            skLineSegment(sketch, "E9.115.0", {"start": v(31.82, 32.8) * mm, "end": v(32.83, 31.78) * mm});
            skLineSegment(sketch, "E9.116.0", {"start": v(30.06, 34.41) * mm, "end": v(31.12, 33.46) * mm});
            skLineSegment(sketch, "E9.117.0", {"start": v(28.22, 35.94) * mm, "end": v(29.33, 35.04) * mm});
            skLineSegment(sketch, "E9.118.0", {"start": v(26.3, 37.37) * mm, "end": v(27.45, 36.53) * mm});
            skLineSegment(sketch, "E9.119.0", {"start": v(24.3, 38.7) * mm, "end": v(25.5, 37.92) * mm});
            skSolve(sketch);
        }
        {
            var Q0;
            Q0=makeQuery(id+"F2.imprint","IMPRINT",FACE,{"disambiguationData":[TD([[makeQuery(id+"F2.imprint","IMPRINT",EDGE,{"derivedFrom":sQuery(id+"F2.wireOp",EDGE,"E6.51.0")}),1.0]])]});
            var Q1;
            Q1=makeQuery(id+"F2.imprint","IMPRINT",FACE,{"disambiguationData":[TD([[makeQuery(id+"F2.imprint","IMPRINT",EDGE,{"derivedFrom":sQuery(id+"F2.wireOp",EDGE,"E6.52.0")}),1.0]])]});
            var Q2;
            Q2=makeQuery(id+"F2.imprint","IMPRINT",FACE,{"disambiguationData":[TD([[makeQuery(id+"F2.imprint","IMPRINT",EDGE,{"derivedFrom":sQuery(id+"F2.wireOp",EDGE,"E6.53.0")}),1.0]])]});
            var Q3;
            Q3=makeQuery(id+"F2.imprint","IMPRINT",FACE,{"disambiguationData":[TD([[makeQuery(id+"F2.imprint","IMPRINT",EDGE,{"derivedFrom":sQuery(id+"F2.wireOp",EDGE,"E6.54.0")}),1.0]])]});
            var Q4;
            Q4=makeQuery(id+"F2.imprint","IMPRINT",FACE,{"disambiguationData":[TD([[makeQuery(id+"F2.imprint","IMPRINT",EDGE,{"derivedFrom":sQuery(id+"F2.wireOp",EDGE,"E6.55.0")}),1.0]])]});
            var Q5;
            Q5=makeQuery(id+"F2.imprint","IMPRINT",FACE,{"disambiguationData":[TD([[makeQuery(id+"F2.imprint","IMPRINT",EDGE,{"derivedFrom":sQuery(id+"F2.wireOp",EDGE,"E6.56.0")}),1.0]])]});
            var Q6;
            Q6=makeQuery(id+"F2.imprint","IMPRINT",FACE,{"disambiguationData":[TD([[makeQuery(id+"F2.imprint","IMPRINT",EDGE,{"derivedFrom":sQuery(id+"F2.wireOp",EDGE,"E6.57.0")}),1.0]])]});
            var Q7;
            Q7=makeQuery(id+"F2.imprint","IMPRINT",FACE,{"disambiguationData":[TD([[makeQuery(id+"F2.imprint","IMPRINT",EDGE,{"derivedFrom":sQuery(id+"F2.wireOp",EDGE,"E6.58.0")}),1.0]])]});
            var Q8;
            Q8=makeQuery(id+"F2.imprint","IMPRINT",FACE,{"disambiguationData":[TD([[makeQuery(id+"F2.imprint","IMPRINT",EDGE,{"derivedFrom":sQuery(id+"F2.wireOp",EDGE,"E6.59.0")}),1.0]])]});
            var Q9;
            Q9=makeQuery(id+"F2.imprint","IMPRINT",FACE,{"disambiguationData":[TD([[makeQuery(id+"F2.imprint","IMPRINT",EDGE,{"derivedFrom":sQuery(id+"F2.wireOp",EDGE,"E6.60.0")}),1.0]])]});
            var Q10;
            Q10=makeQuery(id+"F2.imprint","IMPRINT",FACE,{"disambiguationData":[TD([[makeQuery(id+"F2.imprint","IMPRINT",EDGE,{"derivedFrom":sQuery(id+"F2.wireOp",EDGE,"E6.61.0")}),1.0]])]});
            var Q11;
            Q11=makeQuery(id+"F2.imprint","IMPRINT",FACE,{"disambiguationData":[TD([[makeQuery(id+"F2.imprint","IMPRINT",EDGE,{"derivedFrom":sQuery(id+"F2.wireOp",EDGE,"E6.62.0")}),1.0]])]});
            var Q12;
            Q12=makeQuery(id+"F2.imprint","IMPRINT",FACE,{"disambiguationData":[TD([[makeQuery(id+"F2.imprint","IMPRINT",EDGE,{"derivedFrom":sQuery(id+"F2.wireOp",EDGE,"E6.63.0")}),1.0]])]});
            var Q13;
            Q13=makeQuery(id+"F2.imprint","IMPRINT",FACE,{"disambiguationData":[TD([[makeQuery(id+"F2.imprint","IMPRINT",EDGE,{"derivedFrom":sQuery(id+"F2.wireOp",EDGE,"E6.64.0")}),1.0]])]});
            var Q14;
            Q14=makeQuery(id+"F2.imprint","IMPRINT",FACE,{"disambiguationData":[TD([[makeQuery(id+"F2.imprint","IMPRINT",EDGE,{"derivedFrom":sQuery(id+"F2.wireOp",EDGE,"E6.65.0")}),1.0]])]});
            var Q15;
            Q15=makeQuery(id+"F2.imprint","IMPRINT",FACE,{"disambiguationData":[TD([[makeQuery(id+"F2.imprint","IMPRINT",EDGE,{"derivedFrom":sQuery(id+"F2.wireOp",EDGE,"E6.66.0")}),1.0]])]});
            var Q16;
            Q16=makeQuery(id+"F2.imprint","IMPRINT",FACE,{"disambiguationData":[TD([[makeQuery(id+"F2.imprint","IMPRINT",EDGE,{"derivedFrom":sQuery(id+"F2.wireOp",EDGE,"E6.67.0")}),1.0]])]});
            var Q17;
            Q17=makeQuery(id+"F2.imprint","IMPRINT",FACE,{"disambiguationData":[TD([[makeQuery(id+"F2.imprint","IMPRINT",EDGE,{"derivedFrom":sQuery(id+"F2.wireOp",EDGE,"E6.68.0")}),1.0]])]});
            var Q18;
            Q18=makeQuery(id+"F2.imprint","IMPRINT",FACE,{"disambiguationData":[TD([[makeQuery(id+"F2.imprint","IMPRINT",EDGE,{"derivedFrom":sQuery(id+"F2.wireOp",EDGE,"E6.69.0")}),1.0]])]});
            var Q19;
            Q19=makeQuery(id+"F2.imprint","IMPRINT",FACE,{"disambiguationData":[TD([[makeQuery(id+"F2.imprint","IMPRINT",EDGE,{"derivedFrom":sQuery(id+"F2.wireOp",EDGE,"E6.70.0")}),1.0]])]});
            var Q20;
            Q20=makeQuery(id+"F2.imprint","IMPRINT",FACE,{"disambiguationData":[TD([[makeQuery(id+"F2.imprint","IMPRINT",EDGE,{"derivedFrom":sQuery(id+"F2.wireOp",EDGE,"E6.71.0")}),1.0]])]});
            var Q21;
            Q21=makeQuery(id+"F2.imprint","IMPRINT",FACE,{"disambiguationData":[TD([[makeQuery(id+"F2.imprint","IMPRINT",EDGE,{"derivedFrom":sQuery(id+"F2.wireOp",EDGE,"E6.72.0")}),1.0]])]});
            var Q22;
            Q22=makeQuery(id+"F2.imprint","IMPRINT",FACE,{"disambiguationData":[TD([[makeQuery(id+"F2.imprint","IMPRINT",EDGE,{"derivedFrom":sQuery(id+"F2.wireOp",EDGE,"E6.73.0")}),1.0]])]});
            var Q23;
            Q23=makeQuery(id+"F2.imprint","IMPRINT",FACE,{"disambiguationData":[TD([[makeQuery(id+"F2.imprint","IMPRINT",EDGE,{"derivedFrom":sQuery(id+"F2.wireOp",EDGE,"E6.74.0")}),1.0]])]});
            var Q24;
            Q24=makeQuery(id+"F2.imprint","IMPRINT",FACE,{"disambiguationData":[TD([[makeQuery(id+"F2.imprint","IMPRINT",EDGE,{"derivedFrom":sQuery(id+"F2.wireOp",EDGE,"E6.75.0")}),1.0]])]});
            var Q25;
            Q25=makeQuery(id+"F2.imprint","IMPRINT",FACE,{"disambiguationData":[TD([[makeQuery(id+"F2.imprint","IMPRINT",EDGE,{"derivedFrom":sQuery(id+"F2.wireOp",EDGE,"E6.76.0")}),1.0]])]});
            var Q26;
            Q26=makeQuery(id+"F2.imprint","IMPRINT",FACE,{"disambiguationData":[TD([[makeQuery(id+"F2.imprint","IMPRINT",EDGE,{"derivedFrom":sQuery(id+"F2.wireOp",EDGE,"E6.77.0")}),1.0]])]});
            var Q27;
            Q27=makeQuery(id+"F2.imprint","IMPRINT",FACE,{"disambiguationData":[TD([[makeQuery(id+"F2.imprint","IMPRINT",EDGE,{"derivedFrom":sQuery(id+"F2.wireOp",EDGE,"E6.78.0")}),1.0]])]});
            var Q28;
            Q28=makeQuery(id+"F2.imprint","IMPRINT",FACE,{"disambiguationData":[TD([[makeQuery(id+"F2.imprint","IMPRINT",EDGE,{"derivedFrom":sQuery(id+"F2.wireOp",EDGE,"E6.79.0")}),1.0]])]});
            var Q29;
            Q29=makeQuery(id+"F2.imprint","IMPRINT",FACE,{"disambiguationData":[TD([[makeQuery(id+"F2.imprint","IMPRINT",EDGE,{"derivedFrom":sQuery(id+"F2.wireOp",EDGE,"E6.80.0")}),1.0]])]});
            var Q30;
            Q30=makeQuery(id+"F2.imprint","IMPRINT",FACE,{"disambiguationData":[TD([[makeQuery(id+"F2.imprint","IMPRINT",EDGE,{"derivedFrom":sQuery(id+"F2.wireOp",EDGE,"E6.81.0")}),1.0]])]});
            var Q31;
            Q31=makeQuery(id+"F2.imprint","IMPRINT",FACE,{"disambiguationData":[TD([[makeQuery(id+"F2.imprint","IMPRINT",EDGE,{"derivedFrom":sQuery(id+"F2.wireOp",EDGE,"E6.82.0")}),1.0]])]});
            var Q32;
            Q32=makeQuery(id+"F2.imprint","IMPRINT",FACE,{"disambiguationData":[TD([[makeQuery(id+"F2.imprint","IMPRINT",EDGE,{"derivedFrom":sQuery(id+"F2.wireOp",EDGE,"E6.83.0")}),1.0]])]});
            var Q33;
            Q33=makeQuery(id+"F2.imprint","IMPRINT",FACE,{"disambiguationData":[TD([[makeQuery(id+"F2.imprint","IMPRINT",EDGE,{"derivedFrom":sQuery(id+"F2.wireOp",EDGE,"E6.84.0")}),1.0]])]});
            var Q34;
            Q34=makeQuery(id+"F2.imprint","IMPRINT",FACE,{"disambiguationData":[TD([[makeQuery(id+"F2.imprint","IMPRINT",EDGE,{"derivedFrom":sQuery(id+"F2.wireOp",EDGE,"E6.85.0")}),1.0]])]});
            var Q35;
            Q35=makeQuery(id+"F2.imprint","IMPRINT",FACE,{"disambiguationData":[TD([[makeQuery(id+"F2.imprint","IMPRINT",EDGE,{"derivedFrom":sQuery(id+"F2.wireOp",EDGE,"E6.86.0")}),1.0]])]});
            var Q36;
            Q36=makeQuery(id+"F2.imprint","IMPRINT",FACE,{"disambiguationData":[TD([[makeQuery(id+"F2.imprint","IMPRINT",EDGE,{"derivedFrom":sQuery(id+"F2.wireOp",EDGE,"E6.87.0")}),1.0]])]});
            var Q37;
            Q37=makeQuery(id+"F2.imprint","IMPRINT",FACE,{"disambiguationData":[TD([[makeQuery(id+"F2.imprint","IMPRINT",EDGE,{"derivedFrom":sQuery(id+"F2.wireOp",EDGE,"E6.88.0")}),1.0]])]});
            var Q38;
            Q38=makeQuery(id+"F2.imprint","IMPRINT",FACE,{"disambiguationData":[TD([[makeQuery(id+"F2.imprint","IMPRINT",EDGE,{"derivedFrom":sQuery(id+"F2.wireOp",EDGE,"E6.89.0")}),1.0]])]});
            var Q39;
            Q39=makeQuery(id+"F2.imprint","IMPRINT",FACE,{"disambiguationData":[TD([[makeQuery(id+"F2.imprint","IMPRINT",EDGE,{"derivedFrom":sQuery(id+"F2.wireOp",EDGE,"E6.90.0")}),1.0]])]});
            var Q40;
            Q40=makeQuery(id+"F2.imprint","IMPRINT",FACE,{"disambiguationData":[TD([[makeQuery(id+"F2.imprint","IMPRINT",EDGE,{"derivedFrom":sQuery(id+"F2.wireOp",EDGE,"E6.91.0")}),1.0]])]});
            var Q41;
            Q41=makeQuery(id+"F2.imprint","IMPRINT",FACE,{"disambiguationData":[TD([[makeQuery(id+"F2.imprint","IMPRINT",EDGE,{"derivedFrom":sQuery(id+"F2.wireOp",EDGE,"E6.92.0")}),1.0]])]});
            var Q42;
            Q42=makeQuery(id+"F2.imprint","IMPRINT",FACE,{"disambiguationData":[TD([[makeQuery(id+"F2.imprint","IMPRINT",EDGE,{"derivedFrom":sQuery(id+"F2.wireOp",EDGE,"E6.93.0")}),1.0]])]});
            var Q43;
            Q43=makeQuery(id+"F2.imprint","IMPRINT",FACE,{"disambiguationData":[TD([[makeQuery(id+"F2.imprint","IMPRINT",EDGE,{"derivedFrom":sQuery(id+"F2.wireOp",EDGE,"E6.94.0")}),1.0]])]});
            var Q44;
            Q44=makeQuery(id+"F2.imprint","IMPRINT",FACE,{"disambiguationData":[TD([[makeQuery(id+"F2.imprint","IMPRINT",EDGE,{"derivedFrom":sQuery(id+"F2.wireOp",EDGE,"E6.95.0")}),1.0]])]});
            var Q45;
            Q45=makeQuery(id+"F2.imprint","IMPRINT",FACE,{"disambiguationData":[TD([[makeQuery(id+"F2.imprint","IMPRINT",EDGE,{"derivedFrom":sQuery(id+"F2.wireOp",EDGE,"E6.96.0")}),1.0]])]});
            var Q46;
            Q46=makeQuery(id+"F2.imprint","IMPRINT",FACE,{"disambiguationData":[TD([[makeQuery(id+"F2.imprint","IMPRINT",EDGE,{"derivedFrom":sQuery(id+"F2.wireOp",EDGE,"E6.97.0")}),1.0]])]});
            var Q47;
            Q47=makeQuery(id+"F2.imprint","IMPRINT",FACE,{"disambiguationData":[TD([[makeQuery(id+"F2.imprint","IMPRINT",EDGE,{"derivedFrom":sQuery(id+"F2.wireOp",EDGE,"E6.98.0")}),1.0]])]});
            var Q48;
            Q48=makeQuery(id+"F2.imprint","IMPRINT",FACE,{"disambiguationData":[TD([[makeQuery(id+"F2.imprint","IMPRINT",EDGE,{"derivedFrom":sQuery(id+"F2.wireOp",EDGE,"E6.99.0")}),1.0]])]});
            var Q49;
            Q49=makeQuery(id+"F2.imprint","IMPRINT",FACE,{"disambiguationData":[TD([[makeQuery(id+"F2.imprint","IMPRINT",EDGE,{"derivedFrom":sQuery(id+"F2.wireOp",EDGE,"E6.100.0")}),1.0]])]});
            var Q50;
            Q50=makeQuery(id+"F2.imprint","IMPRINT",FACE,{"disambiguationData":[TD([[makeQuery(id+"F2.imprint","IMPRINT",EDGE,{"derivedFrom":sQuery(id+"F2.wireOp",EDGE,"E6.101.0")}),1.0]])]});
            var Q51;
            Q51=makeQuery(id+"F2.imprint","IMPRINT",FACE,{"disambiguationData":[TD([[makeQuery(id+"F2.imprint","IMPRINT",EDGE,{"derivedFrom":sQuery(id+"F2.wireOp",EDGE,"E6.102.0")}),1.0]])]});
            var Q52;
            Q52=makeQuery(id+"F2.imprint","IMPRINT",FACE,{"disambiguationData":[TD([[makeQuery(id+"F2.imprint","IMPRINT",EDGE,{"derivedFrom":sQuery(id+"F2.wireOp",EDGE,"E6.103.0")}),1.0]])]});
            var Q53;
            Q53=makeQuery(id+"F2.imprint","IMPRINT",FACE,{"disambiguationData":[TD([[makeQuery(id+"F2.imprint","IMPRINT",EDGE,{"derivedFrom":sQuery(id+"F2.wireOp",EDGE,"E6.104.0")}),1.0]])]});
            var Q54;
            Q54=makeQuery(id+"F2.imprint","IMPRINT",FACE,{"disambiguationData":[TD([[makeQuery(id+"F2.imprint","IMPRINT",EDGE,{"derivedFrom":sQuery(id+"F2.wireOp",EDGE,"E6.105.0")}),1.0]])]});
            var Q55;
            Q55=makeQuery(id+"F2.imprint","IMPRINT",FACE,{"disambiguationData":[TD([[makeQuery(id+"F2.imprint","IMPRINT",EDGE,{"derivedFrom":sQuery(id+"F2.wireOp",EDGE,"E6.106.0")}),1.0]])]});
            var Q56;
            Q56=makeQuery(id+"F2.imprint","IMPRINT",FACE,{"disambiguationData":[TD([[makeQuery(id+"F2.imprint","IMPRINT",EDGE,{"derivedFrom":sQuery(id+"F2.wireOp",EDGE,"E6.107.0")}),1.0]])]});
            var Q57;
            Q57=makeQuery(id+"F2.imprint","IMPRINT",FACE,{"disambiguationData":[TD([[makeQuery(id+"F2.imprint","IMPRINT",EDGE,{"derivedFrom":sQuery(id+"F2.wireOp",EDGE,"E6.108.0")}),1.0]])]});
            var Q58;
            Q58=makeQuery(id+"F2.imprint","IMPRINT",FACE,{"disambiguationData":[TD([[makeQuery(id+"F2.imprint","IMPRINT",EDGE,{"derivedFrom":sQuery(id+"F2.wireOp",EDGE,"E6.109.0")}),1.0]])]});
            var Q59;
            Q59=makeQuery(id+"F2.imprint","IMPRINT",FACE,{"disambiguationData":[TD([[makeQuery(id+"F2.imprint","IMPRINT",EDGE,{"derivedFrom":sQuery(id+"F2.wireOp",EDGE,"E6.110.0")}),1.0]])]});
            var Q60;
            Q60=makeQuery(id+"F2.imprint","IMPRINT",FACE,{"disambiguationData":[TD([[makeQuery(id+"F2.imprint","IMPRINT",EDGE,{"derivedFrom":sQuery(id+"F2.wireOp",EDGE,"E6.111.0")}),1.0]])]});
            var Q61;
            Q61=makeQuery(id+"F2.imprint","IMPRINT",FACE,{"disambiguationData":[TD([[makeQuery(id+"F2.imprint","IMPRINT",EDGE,{"derivedFrom":sQuery(id+"F2.wireOp",EDGE,"E6.112.0")}),1.0]])]});
            var Q62;
            Q62=makeQuery(id+"F2.imprint","IMPRINT",FACE,{"disambiguationData":[TD([[makeQuery(id+"F2.imprint","IMPRINT",EDGE,{"derivedFrom":sQuery(id+"F2.wireOp",EDGE,"E6.113.0")}),1.0]])]});
            var Q63;
            Q63=makeQuery(id+"F2.imprint","IMPRINT",FACE,{"disambiguationData":[TD([[makeQuery(id+"F2.imprint","IMPRINT",EDGE,{"derivedFrom":sQuery(id+"F2.wireOp",EDGE,"E6.114.0")}),1.0]])]});
            var Q64;
            Q64=makeQuery(id+"F2.imprint","IMPRINT",FACE,{"disambiguationData":[TD([[makeQuery(id+"F2.imprint","IMPRINT",EDGE,{"derivedFrom":sQuery(id+"F2.wireOp",EDGE,"E6.115.0")}),1.0]])]});
            var Q65;
            Q65=makeQuery(id+"F2.imprint","IMPRINT",FACE,{"disambiguationData":[TD([[makeQuery(id+"F2.imprint","IMPRINT",EDGE,{"derivedFrom":sQuery(id+"F2.wireOp",EDGE,"E6.116.0")}),1.0]])]});
            var Q66;
            Q66=makeQuery(id+"F2.imprint","IMPRINT",FACE,{"disambiguationData":[TD([[makeQuery(id+"F2.imprint","IMPRINT",EDGE,{"derivedFrom":sQuery(id+"F2.wireOp",EDGE,"E6.117.0")}),1.0]])]});
            var Q67;
            Q67=makeQuery(id+"F2.imprint","IMPRINT",FACE,{"disambiguationData":[TD([[makeQuery(id+"F2.imprint","IMPRINT",EDGE,{"derivedFrom":sQuery(id+"F2.wireOp",EDGE,"E6.118.0")}),1.0]])]});
            var Q68;
            Q68=makeQuery(id+"F2.imprint","IMPRINT",FACE,{"disambiguationData":[TD([[makeQuery(id+"F2.imprint","IMPRINT",EDGE,{"derivedFrom":sQuery(id+"F2.wireOp",EDGE,"E6.119.0")}),1.0]])]});
            var Q69;
            Q69=makeQuery(id+"F2.imprint","IMPRINT",FACE,{"disambiguationData":[TD([[makeQuery(id+"F2.imprint","IMPRINT",EDGE,{"derivedFrom":sQuery(id+"F2.wireOp",EDGE,"E4")}),1.0]])]});
            var Q70;
            Q70=makeQuery(id+"F2.imprint","IMPRINT",FACE,{"disambiguationData":[TD([[makeQuery(id+"F2.imprint","IMPRINT",EDGE,{"derivedFrom":sQuery(id+"F2.wireOp",EDGE,"E6.1.0")}),1.0]])]});
            var Q71;
            Q71=makeQuery(id+"F2.imprint","IMPRINT",FACE,{"disambiguationData":[TD([[makeQuery(id+"F2.imprint","IMPRINT",EDGE,{"derivedFrom":sQuery(id+"F2.wireOp",EDGE,"E6.2.0")}),1.0]])]});
            var Q72;
            Q72=makeQuery(id+"F2.imprint","IMPRINT",FACE,{"disambiguationData":[TD([[makeQuery(id+"F2.imprint","IMPRINT",EDGE,{"derivedFrom":sQuery(id+"F2.wireOp",EDGE,"E6.3.0")}),1.0]])]});
            var Q73;
            Q73=makeQuery(id+"F2.imprint","IMPRINT",FACE,{"disambiguationData":[TD([[makeQuery(id+"F2.imprint","IMPRINT",EDGE,{"derivedFrom":sQuery(id+"F2.wireOp",EDGE,"E6.4.0")}),1.0]])]});
            var Q74;
            Q74=makeQuery(id+"F2.imprint","IMPRINT",FACE,{"disambiguationData":[TD([[makeQuery(id+"F2.imprint","IMPRINT",EDGE,{"derivedFrom":sQuery(id+"F2.wireOp",EDGE,"E6.5.0")}),1.0]])]});
            var Q75;
            Q75=makeQuery(id+"F2.imprint","IMPRINT",FACE,{"disambiguationData":[TD([[makeQuery(id+"F2.imprint","IMPRINT",EDGE,{"derivedFrom":sQuery(id+"F2.wireOp",EDGE,"E6.6.0")}),1.0]])]});
            var Q76;
            Q76=makeQuery(id+"F2.imprint","IMPRINT",FACE,{"disambiguationData":[TD([[makeQuery(id+"F2.imprint","IMPRINT",EDGE,{"derivedFrom":sQuery(id+"F2.wireOp",EDGE,"E6.7.0")}),1.0]])]});
            var Q77;
            Q77=makeQuery(id+"F2.imprint","IMPRINT",FACE,{"disambiguationData":[TD([[makeQuery(id+"F2.imprint","IMPRINT",EDGE,{"derivedFrom":sQuery(id+"F2.wireOp",EDGE,"E6.8.0")}),1.0]])]});
            var Q78;
            Q78=makeQuery(id+"F2.imprint","IMPRINT",FACE,{"disambiguationData":[TD([[makeQuery(id+"F2.imprint","IMPRINT",EDGE,{"derivedFrom":sQuery(id+"F2.wireOp",EDGE,"E6.9.0")}),1.0]])]});
            var Q79;
            Q79=makeQuery(id+"F2.imprint","IMPRINT",FACE,{"disambiguationData":[TD([[makeQuery(id+"F2.imprint","IMPRINT",EDGE,{"derivedFrom":sQuery(id+"F2.wireOp",EDGE,"E6.10.0")}),1.0]])]});
            var Q80;
            Q80=makeQuery(id+"F2.imprint","IMPRINT",FACE,{"disambiguationData":[TD([[makeQuery(id+"F2.imprint","IMPRINT",EDGE,{"derivedFrom":sQuery(id+"F2.wireOp",EDGE,"E6.11.0")}),1.0]])]});
            var Q81;
            Q81=makeQuery(id+"F2.imprint","IMPRINT",FACE,{"disambiguationData":[TD([[makeQuery(id+"F2.imprint","IMPRINT",EDGE,{"derivedFrom":sQuery(id+"F2.wireOp",EDGE,"E6.12.0")}),1.0]])]});
            var Q82;
            Q82=makeQuery(id+"F2.imprint","IMPRINT",FACE,{"disambiguationData":[TD([[makeQuery(id+"F2.imprint","IMPRINT",EDGE,{"derivedFrom":sQuery(id+"F2.wireOp",EDGE,"E6.13.0")}),1.0]])]});
            var Q83;
            Q83=makeQuery(id+"F2.imprint","IMPRINT",FACE,{"disambiguationData":[TD([[makeQuery(id+"F2.imprint","IMPRINT",EDGE,{"derivedFrom":sQuery(id+"F2.wireOp",EDGE,"E6.14.0")}),1.0]])]});
            var Q84;
            Q84=makeQuery(id+"F2.imprint","IMPRINT",FACE,{"disambiguationData":[TD([[makeQuery(id+"F2.imprint","IMPRINT",EDGE,{"derivedFrom":sQuery(id+"F2.wireOp",EDGE,"E6.15.0")}),1.0]])]});
            var Q85;
            Q85=makeQuery(id+"F2.imprint","IMPRINT",FACE,{"disambiguationData":[TD([[makeQuery(id+"F2.imprint","IMPRINT",EDGE,{"derivedFrom":sQuery(id+"F2.wireOp",EDGE,"E6.16.0")}),1.0]])]});
            var Q86;
            Q86=makeQuery(id+"F2.imprint","IMPRINT",FACE,{"disambiguationData":[TD([[makeQuery(id+"F2.imprint","IMPRINT",EDGE,{"derivedFrom":sQuery(id+"F2.wireOp",EDGE,"E6.17.0")}),1.0]])]});
            var Q87;
            Q87=makeQuery(id+"F2.imprint","IMPRINT",FACE,{"disambiguationData":[TD([[makeQuery(id+"F2.imprint","IMPRINT",EDGE,{"derivedFrom":sQuery(id+"F2.wireOp",EDGE,"E6.18.0")}),1.0]])]});
            var Q88;
            Q88=makeQuery(id+"F2.imprint","IMPRINT",FACE,{"disambiguationData":[TD([[makeQuery(id+"F2.imprint","IMPRINT",EDGE,{"derivedFrom":sQuery(id+"F2.wireOp",EDGE,"E6.19.0")}),1.0]])]});
            var Q89;
            Q89=makeQuery(id+"F2.imprint","IMPRINT",FACE,{"disambiguationData":[TD([[makeQuery(id+"F2.imprint","IMPRINT",EDGE,{"derivedFrom":sQuery(id+"F2.wireOp",EDGE,"E6.20.0")}),1.0]])]});
            var Q90;
            Q90=makeQuery(id+"F2.imprint","IMPRINT",FACE,{"disambiguationData":[TD([[makeQuery(id+"F2.imprint","IMPRINT",EDGE,{"derivedFrom":sQuery(id+"F2.wireOp",EDGE,"E6.21.0")}),1.0]])]});
            var Q91;
            Q91=makeQuery(id+"F2.imprint","IMPRINT",FACE,{"disambiguationData":[TD([[makeQuery(id+"F2.imprint","IMPRINT",EDGE,{"derivedFrom":sQuery(id+"F2.wireOp",EDGE,"E6.22.0")}),1.0]])]});
            var Q92;
            Q92=makeQuery(id+"F2.imprint","IMPRINT",FACE,{"disambiguationData":[TD([[makeQuery(id+"F2.imprint","IMPRINT",EDGE,{"derivedFrom":sQuery(id+"F2.wireOp",EDGE,"E6.23.0")}),1.0]])]});
            var Q93;
            Q93=makeQuery(id+"F2.imprint","IMPRINT",FACE,{"disambiguationData":[TD([[makeQuery(id+"F2.imprint","IMPRINT",EDGE,{"derivedFrom":sQuery(id+"F2.wireOp",EDGE,"E6.24.0")}),1.0]])]});
            var Q94;
            Q94=makeQuery(id+"F2.imprint","IMPRINT",FACE,{"disambiguationData":[TD([[makeQuery(id+"F2.imprint","IMPRINT",EDGE,{"derivedFrom":sQuery(id+"F2.wireOp",EDGE,"E6.25.0")}),1.0]])]});
            var Q95;
            Q95=makeQuery(id+"F2.imprint","IMPRINT",FACE,{"disambiguationData":[TD([[makeQuery(id+"F2.imprint","IMPRINT",EDGE,{"derivedFrom":sQuery(id+"F2.wireOp",EDGE,"E6.26.0")}),1.0]])]});
            var Q96;
            Q96=makeQuery(id+"F2.imprint","IMPRINT",FACE,{"disambiguationData":[TD([[makeQuery(id+"F2.imprint","IMPRINT",EDGE,{"derivedFrom":sQuery(id+"F2.wireOp",EDGE,"E6.27.0")}),1.0]])]});
            var Q97;
            Q97=makeQuery(id+"F2.imprint","IMPRINT",FACE,{"disambiguationData":[TD([[makeQuery(id+"F2.imprint","IMPRINT",EDGE,{"derivedFrom":sQuery(id+"F2.wireOp",EDGE,"E6.28.0")}),1.0]])]});
            var Q98;
            Q98=makeQuery(id+"F2.imprint","IMPRINT",FACE,{"disambiguationData":[TD([[makeQuery(id+"F2.imprint","IMPRINT",EDGE,{"derivedFrom":sQuery(id+"F2.wireOp",EDGE,"E6.29.0")}),1.0]])]});
            var Q99;
            Q99=makeQuery(id+"F2.imprint","IMPRINT",FACE,{"disambiguationData":[TD([[makeQuery(id+"F2.imprint","IMPRINT",EDGE,{"derivedFrom":sQuery(id+"F2.wireOp",EDGE,"E6.30.0")}),1.0]])]});
            var Q100;
            Q100=makeQuery(id+"F2.imprint","IMPRINT",FACE,{"disambiguationData":[TD([[makeQuery(id+"F2.imprint","IMPRINT",EDGE,{"derivedFrom":sQuery(id+"F2.wireOp",EDGE,"E6.31.0")}),1.0]])]});
            var Q101;
            Q101=makeQuery(id+"F2.imprint","IMPRINT",FACE,{"disambiguationData":[TD([[makeQuery(id+"F2.imprint","IMPRINT",EDGE,{"derivedFrom":sQuery(id+"F2.wireOp",EDGE,"E6.32.0")}),1.0]])]});
            var Q102;
            Q102=makeQuery(id+"F2.imprint","IMPRINT",FACE,{"disambiguationData":[TD([[makeQuery(id+"F2.imprint","IMPRINT",EDGE,{"derivedFrom":sQuery(id+"F2.wireOp",EDGE,"E6.33.0")}),1.0]])]});
            var Q103;
            Q103=makeQuery(id+"F2.imprint","IMPRINT",FACE,{"disambiguationData":[TD([[makeQuery(id+"F2.imprint","IMPRINT",EDGE,{"derivedFrom":sQuery(id+"F2.wireOp",EDGE,"E6.34.0")}),1.0]])]});
            var Q104;
            Q104=makeQuery(id+"F2.imprint","IMPRINT",FACE,{"disambiguationData":[TD([[makeQuery(id+"F2.imprint","IMPRINT",EDGE,{"derivedFrom":sQuery(id+"F2.wireOp",EDGE,"E6.35.0")}),1.0]])]});
            var Q105;
            Q105=makeQuery(id+"F2.imprint","IMPRINT",FACE,{"disambiguationData":[TD([[makeQuery(id+"F2.imprint","IMPRINT",EDGE,{"derivedFrom":sQuery(id+"F2.wireOp",EDGE,"E6.36.0")}),1.0]])]});
            var Q106;
            Q106=makeQuery(id+"F2.imprint","IMPRINT",FACE,{"disambiguationData":[TD([[makeQuery(id+"F2.imprint","IMPRINT",EDGE,{"derivedFrom":sQuery(id+"F2.wireOp",EDGE,"E6.37.0")}),1.0]])]});
            var Q107;
            Q107=makeQuery(id+"F2.imprint","IMPRINT",FACE,{"disambiguationData":[TD([[makeQuery(id+"F2.imprint","IMPRINT",EDGE,{"derivedFrom":sQuery(id+"F2.wireOp",EDGE,"E6.36.0")}),1.0]])]});
            var Q108;
            Q108=makeQuery(id+"F2.imprint","IMPRINT",FACE,{"disambiguationData":[TD([[makeQuery(id+"F2.imprint","IMPRINT",EDGE,{"derivedFrom":sQuery(id+"F2.wireOp",EDGE,"E6.38.0")}),1.0]])]});
            var Q109;
            Q109=makeQuery(id+"F2.imprint","IMPRINT",FACE,{"disambiguationData":[TD([[makeQuery(id+"F2.imprint","IMPRINT",EDGE,{"derivedFrom":sQuery(id+"F2.wireOp",EDGE,"E6.39.0")}),1.0]])]});
            var Q110;
            Q110=makeQuery(id+"F2.imprint","IMPRINT",FACE,{"disambiguationData":[TD([[makeQuery(id+"F2.imprint","IMPRINT",EDGE,{"derivedFrom":sQuery(id+"F2.wireOp",EDGE,"E6.40.0")}),1.0]])]});
            var Q111;
            Q111=makeQuery(id+"F2.imprint","IMPRINT",FACE,{"disambiguationData":[TD([[makeQuery(id+"F2.imprint","IMPRINT",EDGE,{"derivedFrom":sQuery(id+"F2.wireOp",EDGE,"E6.41.0")}),1.0]])]});
            var Q112;
            Q112=makeQuery(id+"F2.imprint","IMPRINT",FACE,{"disambiguationData":[TD([[makeQuery(id+"F2.imprint","IMPRINT",EDGE,{"derivedFrom":sQuery(id+"F2.wireOp",EDGE,"E6.42.0")}),1.0]])]});
            var Q113;
            Q113=makeQuery(id+"F2.imprint","IMPRINT",FACE,{"disambiguationData":[TD([[makeQuery(id+"F2.imprint","IMPRINT",EDGE,{"derivedFrom":sQuery(id+"F2.wireOp",EDGE,"E6.43.0")}),1.0]])]});
            var Q114;
            Q114=makeQuery(id+"F2.imprint","IMPRINT",FACE,{"disambiguationData":[TD([[makeQuery(id+"F2.imprint","IMPRINT",EDGE,{"derivedFrom":sQuery(id+"F2.wireOp",EDGE,"E6.44.0")}),1.0]])]});
            var Q115;
            Q115=makeQuery(id+"F2.imprint","IMPRINT",FACE,{"disambiguationData":[TD([[makeQuery(id+"F2.imprint","IMPRINT",EDGE,{"derivedFrom":sQuery(id+"F2.wireOp",EDGE,"E6.45.0")}),1.0]])]});
            var Q116;
            Q116=makeQuery(id+"F2.imprint","IMPRINT",FACE,{"disambiguationData":[TD([[makeQuery(id+"F2.imprint","IMPRINT",EDGE,{"derivedFrom":sQuery(id+"F2.wireOp",EDGE,"E6.46.0")}),1.0]])]});
            var Q117;
            Q117=makeQuery(id+"F2.imprint","IMPRINT",FACE,{"disambiguationData":[TD([[makeQuery(id+"F2.imprint","IMPRINT",EDGE,{"derivedFrom":sQuery(id+"F2.wireOp",EDGE,"E6.47.0")}),1.0]])]});
            var Q118;
            Q118=makeQuery(id+"F2.imprint","IMPRINT",FACE,{"disambiguationData":[TD([[makeQuery(id+"F2.imprint","IMPRINT",EDGE,{"derivedFrom":sQuery(id+"F2.wireOp",EDGE,"E6.48.0")}),1.0]])]});
            var Q119;
            Q119=makeQuery(id+"F2.imprint","IMPRINT",FACE,{"disambiguationData":[TD([[makeQuery(id+"F2.imprint","IMPRINT",EDGE,{"derivedFrom":sQuery(id+"F2.wireOp",EDGE,"E6.49.0")}),1.0]])]});
            var Q120;
            Q120=makeQuery(id+"F2.imprint","IMPRINT",FACE,{"disambiguationData":[TD([[makeQuery(id+"F2.imprint","IMPRINT",EDGE,{"derivedFrom":sQuery(id+"F2.wireOp",EDGE,"E6.50.0")}),1.0]])]});
            extrude(context, id + "F3", {"entities" : qUnion([Q0, Q1, Q2, Q3, Q4, Q5, Q6, Q7, Q8, Q9, Q10, Q11, Q12, Q13, Q14, Q15, Q16, Q17, Q18, Q19, Q20, Q21, Q22, Q23, Q24, Q25, Q26, Q27, Q28, Q29, Q30, Q31, Q32, Q33, Q34, Q35, Q36, Q37, Q38, Q39, Q40, Q41, Q42, Q43, Q44, Q45, Q46, Q47, Q48, Q49, Q50, Q51, Q52, Q53, Q54, Q55, Q56, Q57, Q58, Q59, Q60, Q61, Q62, Q63, Q64, Q65, Q66, Q67, Q68, Q69, Q70, Q71, Q72, Q73, Q74, Q75, Q76, Q77, Q78, Q79, Q80, Q81, Q82, Q83, Q84, Q85, Q86, Q87, Q88, Q89, Q90, Q91, Q92, Q93, Q94, Q95, Q96, Q97, Q98, Q99, Q100, Q101, Q102, Q103, Q104, Q105, Q106, Q107, Q108, Q109, Q110, Q111, Q112, Q113, Q114, Q115, Q116, Q117, Q118, Q119, Q120]), "operationType" : NewBodyOperationType.ADD, "depth" : 6.3 * mm});
        }
    });
